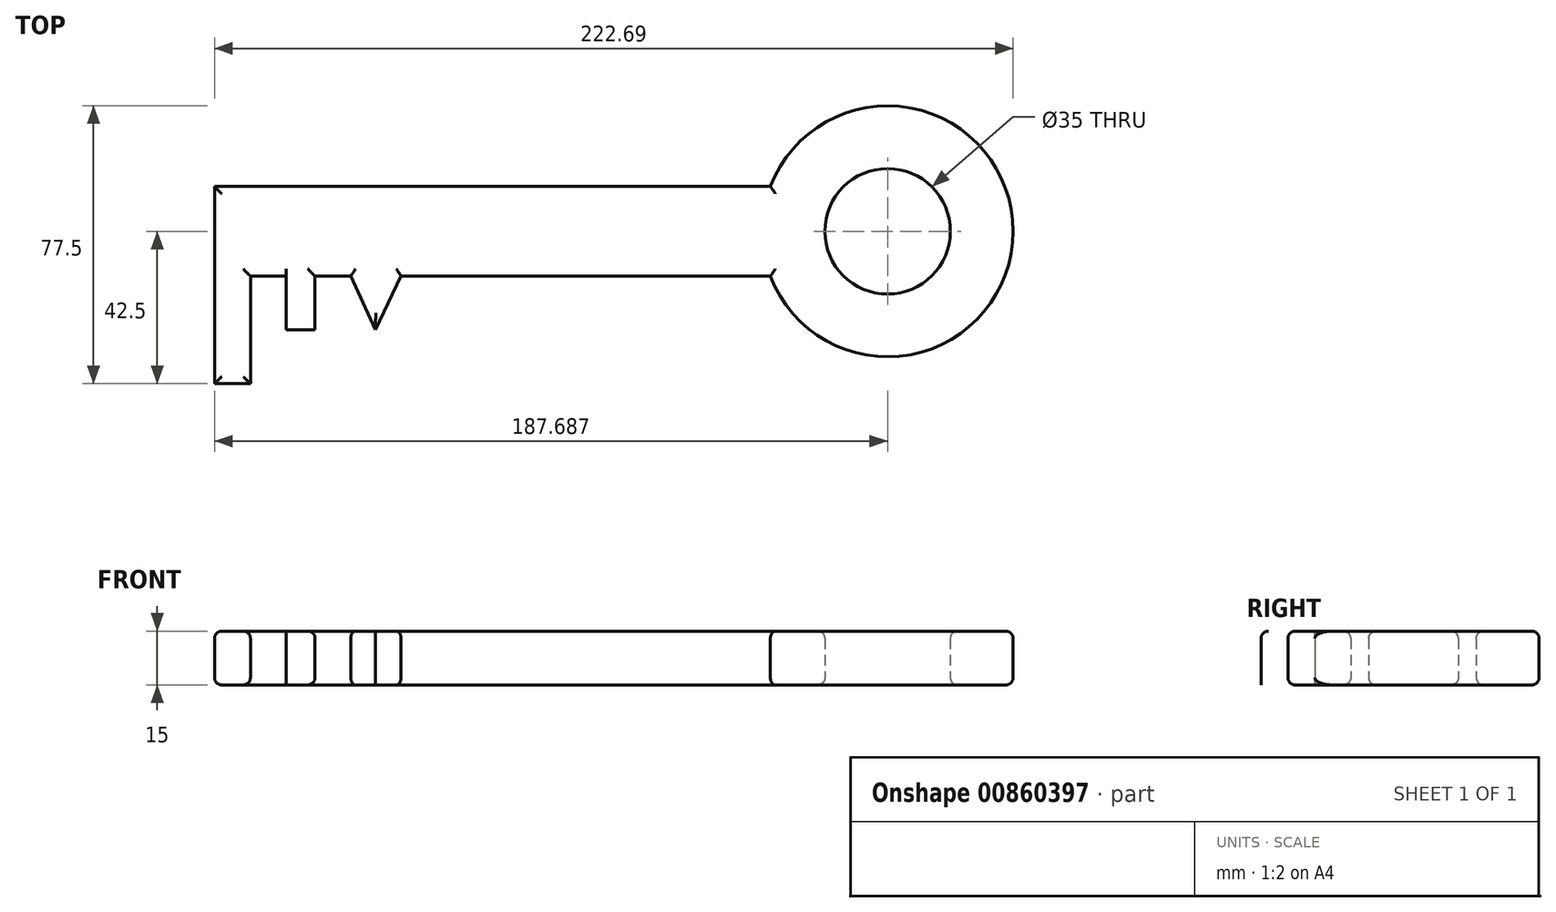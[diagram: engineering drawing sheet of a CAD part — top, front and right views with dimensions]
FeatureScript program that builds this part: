
annotation { "Feature Type Name" : "Feature", "Feature Type Description" : "" }
export const myFeature = defineFeature(function(context is Context, id is Id, definition is map)
    precondition{}
    {
        {
            var Q0;
            Q0=qCreatedBy(makeId("Top.planeOp"),FACE);
            var sketch = newSketch(context, id + "F0", { "sketchPlane" : qUnion([Q0])});
            skLineSegment(sketch, "E0.bottom", {"start": v(-21.33, 12.5) * mm, "end": v(-176.33, 12.5) * mm});
            skLineSegment(sketch, "E0.top", {"start": v(-21.33, -12.5) * mm, "end": v(-176.33, -12.5) * mm});
            skLineSegment(sketch, "E0.left", {"start": v(-21.33, 12.5) * mm, "end": v(-21.33, -12.5) * mm});
            skLineSegment(sketch, "E0.right", {"start": v(-176.33, 12.5) * mm, "end": v(-176.33, -12.5) * mm});
            skLineSegment(sketch, "E1.bottom", {"start": v(-176.33, -12.5) * mm, "end": v(-166.33, -12.5) * mm});
            skLineSegment(sketch, "E1.top", {"start": v(-176.33, -42.5) * mm, "end": v(-166.33, -42.5) * mm});
            skLineSegment(sketch, "E1.left", {"start": v(-176.33, -12.5) * mm, "end": v(-176.33, -42.5) * mm});
            skLineSegment(sketch, "E1.right", {"start": v(-166.33, -12.5) * mm, "end": v(-166.33, -42.5) * mm});
            skLineSegment(sketch, "E2.bottom", {"start": v(-148.33, -12.5) * mm, "end": v(-156.33, -12.5) * mm});
            skLineSegment(sketch, "E2.top", {"start": v(-148.33, -27.5) * mm, "end": v(-156.33, -27.5) * mm});
            skLineSegment(sketch, "E2.left", {"start": v(-148.33, -12.5) * mm, "end": v(-148.33, -27.5) * mm});
            skLineSegment(sketch, "E2.right", {"start": v(-156.33, -12.5) * mm, "end": v(-156.33, -27.5) * mm});
            skLineSegment(sketch, "E3", {"start": v(-138.33, -12.5) * mm, "end": v(-131.42, -27.5) * mm});
            skLineSegment(sketch, "E4", {"start": v(-131.42, -27.5) * mm, "end": v(-124.33, -12.5) * mm});
            skArc(sketch, "E5", {"start": v(-21.33, -12.5) * mm, "mid": v(46.36, 0) * mm, "end": v(-21.33, 12.5) * mm});
            skCircle(sketch, "E6", {"center": v(11.36, 0) * mm, "radius": 17.5 * mm});
            skLineSegment(sketch, "E7", {"start": v(11.36, 0) * mm, "end": v(-176.33, 0) * mm, "construction": true});
            skSolve(sketch);
        }
        {
            var Q0;
            Q0=makeQuery(id+"F0.imprint","IMPRINT",FACE,{"disambiguationData":[TD([[makeQuery(id+"F0.imprint","IMPRINT",EDGE,{"derivedFrom":sQuery(id+"F0.wireOp",EDGE,"E0.bottom")}),1.0]])]});
            var Q1;
            Q1=makeQuery(id+"F0.imprint","IMPRINT",FACE,{"disambiguationData":[TD([[makeQuery(id+"F0.imprint","IMPRINT",EDGE,{"derivedFrom":sQuery(id+"F0.wireOp",EDGE,"E2.top")}),-1.0]])]});
            var Q2;
            Q2=makeQuery(id+"F0.imprint","IMPRINT",FACE,{"disambiguationData":[TD([[makeQuery(id+"F0.imprint","IMPRINT",EDGE,{"derivedFrom":sQuery(id+"F0.wireOp",EDGE,"E1.top")}),1.0]])]});
            var Q3;
            {var subQ0=sQuery(id+"F0.wireOp",EDGE,"E3");Q3=makeQuery(id+"F0.imprint","IMPRINT",FACE,{"disambiguationData":[TD([[makeQuery(id+"F0.imprint","IMPRINT",EDGE,{"derivedFrom":subQ0}),1.0]])]});}
            var Q4;
            Q4=makeQuery(id+"F0.imprint","IMPRINT",FACE,{"disambiguationData":[TD([[makeQuery(id+"F0.imprint","IMPRINT",EDGE,{"derivedFrom":sQuery(id+"F0.wireOp",EDGE,"E0.left")}),1.0]])]});
            extrude(context, id + "F1", {"entities" : qUnion([Q0, Q1, Q2, Q3, Q4]), "depth" : 15 * mm});
        }
        {
            var Q0;
            Q0=makeQuery(id+"F1.opExtrude","CAP_EDGE",EDGE,{"disambiguationData":[OSD([sQuery(id+"F0.wireOp",EDGE,"E0.bottom")])],"isStart":false});
            var Q1;
            {var subQ0=sQuery(id+"F0.wireOp",EDGE,"E0.top");Q1=makeQuery(id+"F1.opExtrude","CAP_EDGE",EDGE,{"disambiguationData":[OSD([subQ0]),TDD([makeQuery(id+"F0.imprint","IMPRINT",EDGE,{"disambiguationData":[TD([[makeQuery(id+"F0.imprint","INTERSECT",VERTEX,{"derivedFrom":[subQ0,sQuery(id+"F0.wireOp",EDGE,"E4")]}),1.0]])],"derivedFrom":subQ0})])],"isStart":false});}
            var Q2;
            Q2=makeQuery(id+"F1.opExtrude","CAP_EDGE",EDGE,{"disambiguationData":[OSD([sQuery(id+"F0.wireOp",EDGE,"E4")])],"isStart":false});
            var Q3;
            Q3=makeQuery(id+"F1.opExtrude","CAP_EDGE",EDGE,{"disambiguationData":[OSD([sQuery(id+"F0.wireOp",EDGE,"E3")])],"isStart":false});
            var Q4;
            Q4=makeQuery(id+"F1.opExtrude","CAP_EDGE",EDGE,{"disambiguationData":[OSD([sQuery(id+"F0.wireOp",EDGE,"E2.left")])],"isStart":false});
            var Q5;
            {var subQ0=sQuery(id+"F0.wireOp",EDGE,"E0.top");Q5=makeQuery(id+"F1.opExtrude","CAP_EDGE",EDGE,{"disambiguationData":[OSD([subQ0]),TDD([makeQuery(id+"F0.imprint","IMPRINT",EDGE,{"disambiguationData":[TD([[makeQuery(id+"F0.imprint","INTERSECT",VERTEX,{"derivedFrom":[subQ0,sQuery(id+"F0.wireOp",EDGE,"E2.left")]}),1.0]])],"derivedFrom":subQ0})])],"isStart":false});}
            var Q6;
            {var subQ0=sQuery(id+"F0.wireOp",EDGE,"E0.top");Q6=makeQuery(id+"F1.opExtrude","CAP_EDGE",EDGE,{"disambiguationData":[OSD([subQ0]),TDD([makeQuery(id+"F0.imprint","IMPRINT",EDGE,{"disambiguationData":[TD([[makeQuery(id+"F0.imprint","INTERSECT",VERTEX,{"derivedFrom":[subQ0,sQuery(id+"F0.wireOp",EDGE,"E2.right")]}),-1.0]])],"derivedFrom":subQ0})])],"isStart":false});}
            var Q7;
            Q7=makeQuery(id+"F1.opExtrude","CAP_EDGE",EDGE,{"disambiguationData":[OSD([sQuery(id+"F0.wireOp",EDGE,"E1.right")])],"isStart":false});
            var Q8;
            Q8=makeQuery(id+"F1.opExtrude","CAP_EDGE",EDGE,{"disambiguationData":[OSD([sQuery(id+"F0.wireOp",EDGE,"E1.top")])],"isStart":false});
            var Q9;
            Q9=makeQuery(id+"F1.opExtrude","CAP_EDGE",EDGE,{"disambiguationData":[OSD([sQuery(id+"F0.wireOp",EDGE,"E0.right"),sQuery(id+"F0.wireOp",EDGE,"E1.left")])],"isStart":false});
            var Q10;
            Q10=makeQuery(id+"F1.opExtrude","CAP_EDGE",EDGE,{"disambiguationData":[OSD([sQuery(id+"F0.wireOp",EDGE,"E5")])],"isStart":false});
            var Q11;
            Q11=makeQuery(id+"F1.opExtrude","CAP_EDGE",EDGE,{"disambiguationData":[OSD([sQuery(id+"F0.wireOp",EDGE,"E6")])],"isStart":false});
            var Q12;
            Q12=makeQuery(id+"F1.opExtrude","CAP_EDGE",EDGE,{"disambiguationData":[OSD([sQuery(id+"F0.wireOp",EDGE,"E0.bottom")])],"isStart":true});
            var Q13;
            {var subQ0=sQuery(id+"F0.wireOp",EDGE,"E0.top");Q13=makeQuery(id+"F1.opExtrude","CAP_EDGE",EDGE,{"disambiguationData":[OSD([subQ0]),TDD([makeQuery(id+"F0.imprint","IMPRINT",EDGE,{"disambiguationData":[TD([[makeQuery(id+"F0.imprint","INTERSECT",VERTEX,{"derivedFrom":[subQ0,sQuery(id+"F0.wireOp",EDGE,"E4")]}),1.0]])],"derivedFrom":subQ0})])],"isStart":true});}
            var Q14;
            Q14=makeQuery(id+"F1.opExtrude","CAP_EDGE",EDGE,{"disambiguationData":[OSD([sQuery(id+"F0.wireOp",EDGE,"E4")])],"isStart":true});
            var Q15;
            {var subQ0=sQuery(id+"F0.wireOp",EDGE,"E0.top");Q15=makeQuery(id+"F1.opExtrude","CAP_EDGE",EDGE,{"disambiguationData":[OSD([subQ0]),TDD([makeQuery(id+"F0.imprint","IMPRINT",EDGE,{"disambiguationData":[TD([[makeQuery(id+"F0.imprint","INTERSECT",VERTEX,{"derivedFrom":[subQ0,sQuery(id+"F0.wireOp",EDGE,"E2.left")]}),1.0]])],"derivedFrom":subQ0})])],"isStart":true});}
            var Q16;
            Q16=makeQuery(id+"F1.opExtrude","CAP_EDGE",EDGE,{"disambiguationData":[OSD([sQuery(id+"F0.wireOp",EDGE,"E3")])],"isStart":true});
            var Q17;
            Q17=makeQuery(id+"F1.opExtrude","CAP_EDGE",EDGE,{"disambiguationData":[OSD([sQuery(id+"F0.wireOp",EDGE,"E2.left")])],"isStart":true});
            var Q18;
            Q18=makeQuery(id+"F1.opExtrude","CAP_EDGE",EDGE,{"disambiguationData":[OSD([sQuery(id+"F0.wireOp",EDGE,"E5")])],"isStart":true});
            var Q19;
            Q19=makeQuery(id+"F1.opExtrude","CAP_EDGE",EDGE,{"disambiguationData":[OSD([sQuery(id+"F0.wireOp",EDGE,"E6")])],"isStart":true});
            var Q20;
            Q20=makeQuery(id+"F1.opExtrude","CAP_EDGE",EDGE,{"disambiguationData":[OSD([sQuery(id+"F0.wireOp",EDGE,"E0.right"),sQuery(id+"F0.wireOp",EDGE,"E1.left")])],"isStart":true});
            var Q21;
            Q21=makeQuery(id+"F1.opExtrude","CAP_EDGE",EDGE,{"disambiguationData":[OSD([sQuery(id+"F0.wireOp",EDGE,"E1.right")])],"isStart":true});
            var Q22;
            {var subQ0=sQuery(id+"F0.wireOp",EDGE,"E0.top");Q22=makeQuery(id+"F1.opExtrude","CAP_EDGE",EDGE,{"disambiguationData":[OSD([subQ0]),TDD([makeQuery(id+"F0.imprint","IMPRINT",EDGE,{"disambiguationData":[TD([[makeQuery(id+"F0.imprint","INTERSECT",VERTEX,{"derivedFrom":[subQ0,sQuery(id+"F0.wireOp",EDGE,"E2.right")]}),-1.0]])],"derivedFrom":subQ0})])],"isStart":true});}
            fillet(context, id + "F2", {"entities" : qUnion([Q0, Q1, Q2, Q3, Q4, Q5, Q6, Q7, Q8, Q9, Q10, Q11, Q12, Q13, Q14, Q15, Q16, Q17, Q18, Q19, Q20, Q21, Q22]), "radius" : 2 * mm, "tangentPropagation" : true, "allowEdgeOverflow" : false});
        }
    });
